# Revit family: Hydration_Station-Haws_Corporation-Brita_Hydration_Surface_Mount
name_source: partatom
category: Specialty Equipment
revit_build: Autodesk Revit MEP 2013 (Build: 20130531_2115(x64)
units: mm (PartAtom-declared; Revit-internal decimal feet)

## types (1)
- Surface Mounted
    Apparent Load = 110 VA
    Assembly Code = D2010800
    Cost Note = For Cost information please visit the Resource tab in the Product Page URL
    Default Elevation = 2' - 6"
    Depth = 0' - 6 15/16"
    Description = Advanced Water Filtration System
    Faucet = Metal-Haws-Stainless Steel-Brushed
    Flow = 1 GPM
    Frequency = 60 Hz
    Height = 2' - 6 1/4"
    Hydration Center = Plastic-Haws-ABS-White
    Inlet Description = Supply Port
    Insert Tray = Plastic-Haws-ABS-Grey
    Installation Instructions = http://www.britahydrationstation.com
    LEED = http://www.britahydrationstation.com
    Manufacturer = Haws Corporation 1455 Kleppe Lane Sparks, NV 89431
    Model = 2000 SM
    Number of Poles = 1
    Outlet Description = Aux Waste Port
    Panel Finish = Metal-Haws-Stainless Steel-Brushed
    Panel Thickness = 0' - 3 1/2"
    Phase = 1
    Power Factor = 1
    Product Documentation Link = http://www.britahydrationstation.com
    Product Page URL = http://www.britahydrationstation.com
    Sanitary Radius = 0' - 0 3/4"
    Series = Brita Hydration Station
    Spec Data = http://www.britahydrationstation.com
    Supply Radius = 0' - 0 3/16"
    Type Comments = Surface Mounted
    URL = http://www.britahydrationstation.com
    Voltage = 110 V
    Width = 1' - 3"

## geometry (parser evidence)
native form markers: Blend x12, Sweep x2
no freeform markers — native parametric forms only
